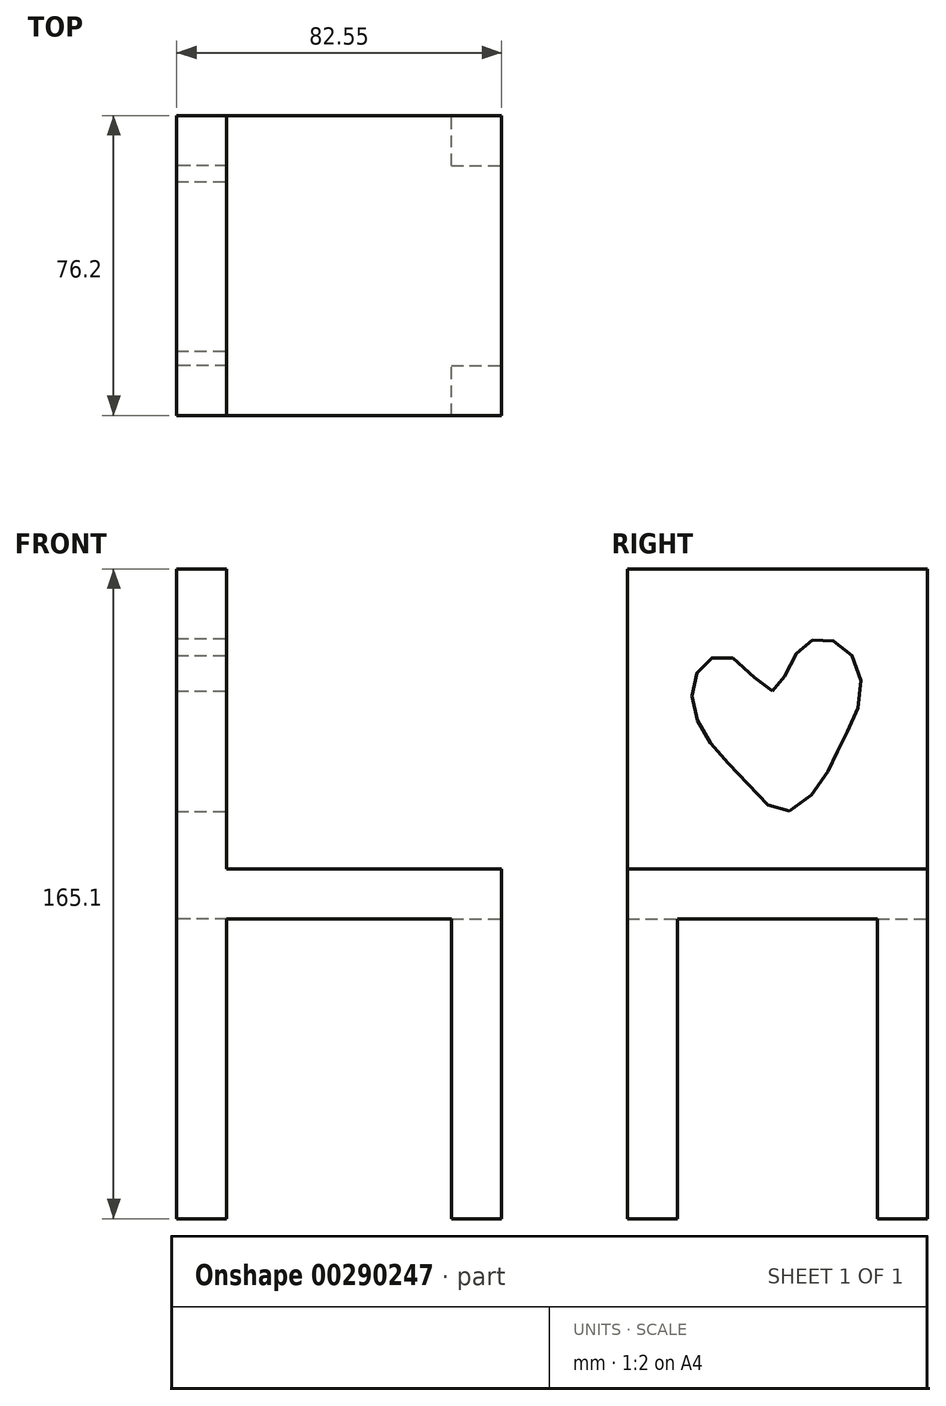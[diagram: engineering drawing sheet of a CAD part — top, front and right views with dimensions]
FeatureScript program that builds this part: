
annotation { "Feature Type Name" : "Feature", "Feature Type Description" : "" }
export const myFeature = defineFeature(function(context is Context, id is Id, definition is map)
    precondition{}
    {
        {
            var Q0;
            Q0=qCreatedBy(makeId("Front.planeOp"),FACE);
            var sketch = newSketch(context, id + "F0", { "sketchPlane" : qUnion([Q0])});
            skLineSegment(sketch, "E0", {"start": v(0, 0) * mm, "end": v(-12.7, 0) * mm});
            skLineSegment(sketch, "E1", {"start": v(0, 0) * mm, "end": v(0, 88.9) * mm});
            skLineSegment(sketch, "E2", {"start": v(-12.7, 0) * mm, "end": v(-12.7, 76.2) * mm});
            skLineSegment(sketch, "E3", {"start": v(-12.7, 76.2) * mm, "end": v(-69.85, 76.2) * mm});
            skLineSegment(sketch, "E4", {"start": v(-69.85, 76.2) * mm, "end": v(-69.85, 0) * mm});
            skLineSegment(sketch, "E5", {"start": v(-69.85, 0) * mm, "end": v(-82.55, 0) * mm});
            skLineSegment(sketch, "E6", {"start": v(-69.85, 88.9) * mm, "end": v(0, 88.9) * mm});
            skPoint(sketch, "E7.start.orphan", {"position": v(-69.85, 152.4) * mm});
            skLineSegment(sketch, "E8", {"start": v(-82.55, 0) * mm, "end": v(-82.55, 165.1) * mm});
            skLineSegment(sketch, "E9", {"start": v(-82.55, 165.1) * mm, "end": v(-69.85, 165.1) * mm});
            skLineSegment(sketch, "E10", {"start": v(-69.85, 165.1) * mm, "end": v(-69.85, 88.9) * mm});
            skSolve(sketch);
        }
        {
            var Q0;
            Q0=makeQuery(id+"F0.imprint","IMPRINT",FACE,{"disambiguationData":[TD([[makeQuery(id+"F0.imprint","IMPRINT",EDGE,{"derivedFrom":sQuery(id+"F0.wireOp",EDGE,"E0")}),-1.0]])]});
            extrude(context, id + "F1", {"entities" : qUnion([Q0]), "depth" : 76.2 * mm});
        }
        {
            var Q0;
            Q0=makeQuery(id+"F1.opExtrude","SWEPT_FACE",FACE,{"disambiguationData":[OSD([sQuery(id+"F0.wireOp",EDGE,"E10")])]});
            var sketch = newSketch(context, id + "F2", { "sketchPlane" : qUnion([Q0])});
            skFitSpline(sketch, "E11", {"points": [v(-39.4, 134.06) * mm, v(-48.88, 142.09) * mm, v(-56.54, 141.36) * mm, v(-59.82, 132.6) * mm, v(-55.44, 121.3) * mm, v(-45.96, 110.72) * mm, v(-36.11, 103.42) * mm, v(-25.9, 112.54) * mm, v(-21.89, 120.93) * mm, v(-17.14, 131.87) * mm, v(-20.06, 144.28) * mm, v(-28.45, 147.2) * mm, v(-34.65, 141.36) * mm, v(-39.4, 134.06) * mm]});
            skSolve(sketch);
        }
        {
            var Q0;
            Q0=makeQuery(id+"F2.imprint","IMPRINT",FACE,{"disambiguationData":[TD([[makeQuery(id+"F2.imprint","IMPRINT",EDGE,{"derivedFrom":sQuery(id+"F2.wireOp",EDGE,"E11")}),1.0]])]});
            extrude(context, id + "F3", {"entities" : qUnion([Q0]), "operationType" : NewBodyOperationType.REMOVE, "oppositeDirection" : true, "depth" : 12.7 * mm});
        }
        {
            var Q0;
            Q0=makeQuery(id+"F1.opExtrude","SWEPT_FACE",FACE,{"disambiguationData":[OSD([sQuery(id+"F0.wireOp",EDGE,"E1")])]});
            var sketch = newSketch(context, id + "F4", { "sketchPlane" : qUnion([Q0])});
            skLineSegment(sketch, "E12", {"start": v(0, 0) * mm, "end": v(-12.7, 0) * mm});
            skLineSegment(sketch, "E13", {"start": v(-12.7, 0) * mm, "end": v(-12.7, 76.2) * mm});
            skLineSegment(sketch, "E14", {"start": v(-12.7, 76.2) * mm, "end": v(-63.5, 76.2) * mm});
            skLineSegment(sketch, "E15", {"start": v(-63.5, 76.2) * mm, "end": v(-63.5, 0) * mm});
            skSolve(sketch);
        }
        {
            var Q0;
            {var subQ0=sQuery(id+"F4.wireOp",EDGE,"E13");Q0=makeQuery(id+"F4.imprint","IMPRINT",FACE,{"disambiguationData":[TD([[makeQuery(id+"F4.imprint","IMPRINT",EDGE,{"derivedFrom":subQ0}),1.0]])]});}
            extrude(context, id + "F5", {"entities" : qUnion([Q0]), "operationType" : NewBodyOperationType.REMOVE, "oppositeDirection" : true, "depth" : 12.7 * mm});
        }
        {
            var Q0;
            Q0=makeQuery(id+"F1.opExtrude","SWEPT_FACE",FACE,{"disambiguationData":[OSD([sQuery(id+"F0.wireOp",EDGE,"E8")])]});
            var sketch = newSketch(context, id + "F6", { "sketchPlane" : qUnion([Q0])});
            skLineSegment(sketch, "E16", {"start": v(0, 0) * mm, "end": v(12.7, 0) * mm});
            skLineSegment(sketch, "E17", {"start": v(12.7, 0) * mm, "end": v(12.7, 76.2) * mm});
            skLineSegment(sketch, "E18", {"start": v(12.7, 76.2) * mm, "end": v(63.5, 76.2) * mm});
            skLineSegment(sketch, "E19", {"start": v(63.5, 76.2) * mm, "end": v(63.5, 0) * mm});
            skLineSegment(sketch, "E20", {"start": v(63.5, 0) * mm, "end": v(76.2, 0) * mm});
            skSolve(sketch);
        }
        {
            var Q0;
            {var subQ0=sQuery(id+"F6.wireOp",EDGE,"E17");Q0=makeQuery(id+"F6.imprint","IMPRINT",FACE,{"disambiguationData":[TD([[makeQuery(id+"F6.imprint","IMPRINT",EDGE,{"derivedFrom":subQ0}),-1.0]])]});}
            extrude(context, id + "F7", {"entities" : qUnion([Q0]), "operationType" : NewBodyOperationType.REMOVE, "oppositeDirection" : true, "depth" : 12.7 * mm});
        }
    });
